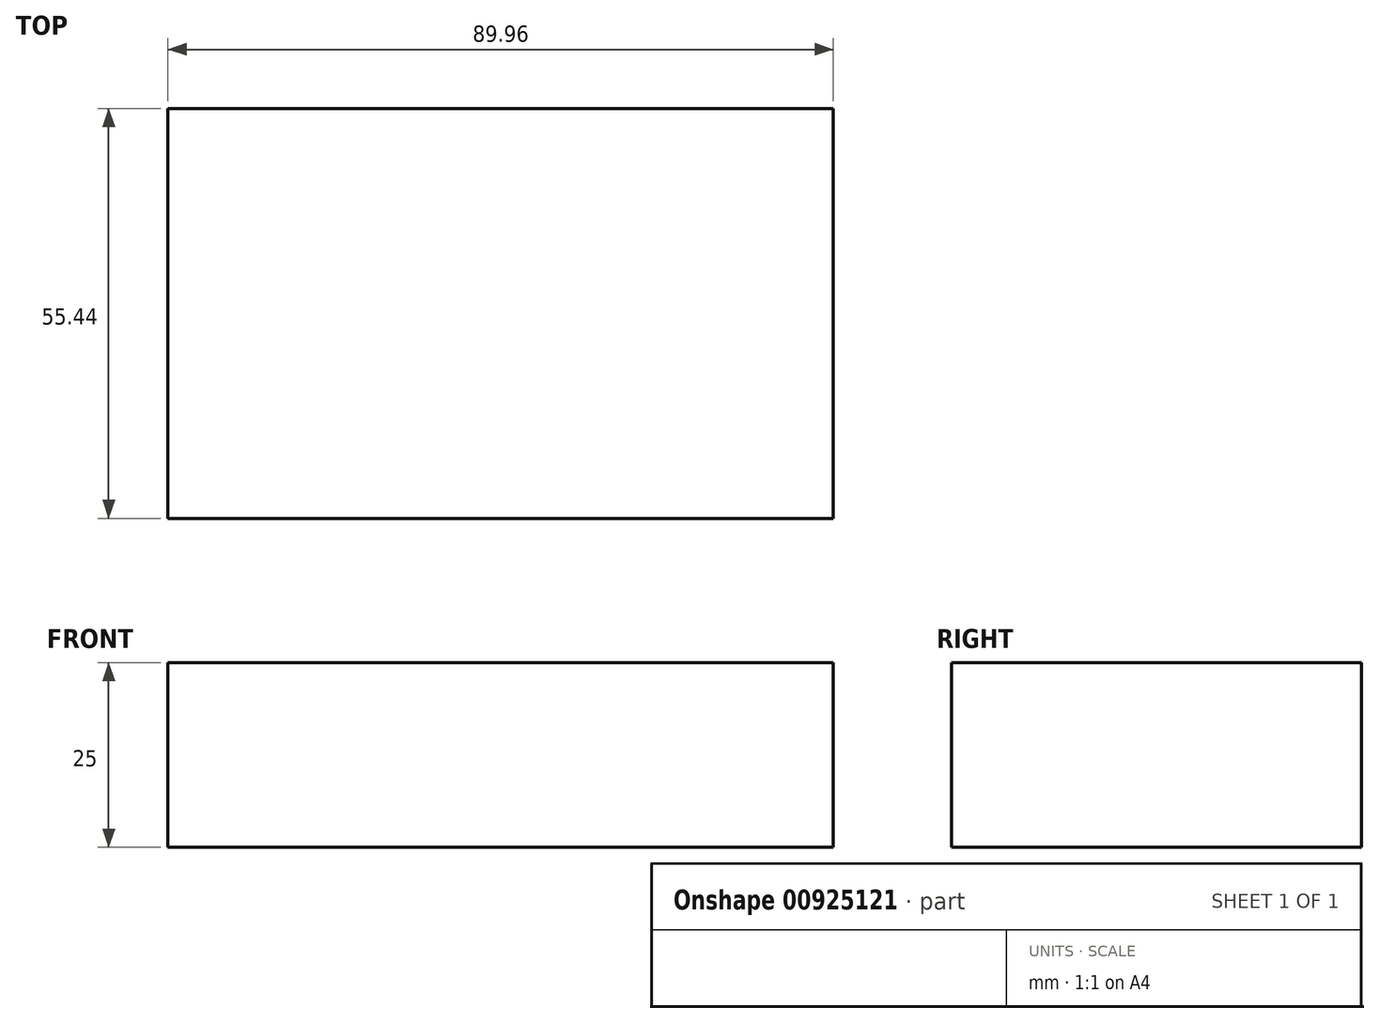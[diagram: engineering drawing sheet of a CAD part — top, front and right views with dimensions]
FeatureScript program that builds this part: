
annotation { "Feature Type Name" : "Feature", "Feature Type Description" : "" }
export const myFeature = defineFeature(function(context is Context, id is Id, definition is map)
    precondition{}
    {
        {
            var Q0;
            Q0=qCreatedBy(makeId("Top.planeOp"),FACE);
            var sketch = newSketch(context, id + "F0", { "sketchPlane" : qUnion([Q0])});
            skLineSegment(sketch, "E0.bottom", {"start": v(-44.98, 27.72) * mm, "end": v(44.98, 27.72) * mm});
            skLineSegment(sketch, "E0.top", {"start": v(-44.98, -27.72) * mm, "end": v(44.98, -27.72) * mm});
            skLineSegment(sketch, "E0.left", {"start": v(-44.98, 27.72) * mm, "end": v(-44.98, -27.72) * mm});
            skLineSegment(sketch, "E0.right", {"start": v(44.98, 27.72) * mm, "end": v(44.98, -27.72) * mm});
            skPoint(sketch, "E0.middle", {"position": v(0, 0) * mm});
            skSolve(sketch);
        }
        {
            var Q0;
            Q0 = qConstructionFilter(qBodyType(qCreatedBy(id + "F0" ,EDGE), BodyType.WIRE), ConstructionObject.NO);
            extrude(context, id + "F1", {"bodyType" : ToolBodyType.SURFACE, "surfaceEntities" : qUnion([Q0]), "depth" : 25 * mm, "offsetDistance" : 25 * mm});
        }
    });
